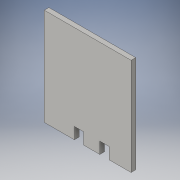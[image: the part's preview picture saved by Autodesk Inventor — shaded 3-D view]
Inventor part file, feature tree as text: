
AUTODESK INVENTOR PART (.ipt)
format: ipt  version: 2016 (Build 200138000, 138)  size: 107,520 bytes
history: native  units: in
note: dims shown in document units (in); Inventor stores cm internally (conversion verified against a paired STEP export)
features: sketch x2, extrude x1
ambient origin geometry x8: Origin, YZ Plane, XZ Plane, XY Plane, X Axis, Y Axis, Z Axis, Center Point
bodies: Solid1 (feature_tree)
feature tree (3):
  sketch  "Sketch1"  dims[d1=10.5in d2=5.125in]
  extrude  "Extrusion1"  Depth=5.125in
  sketch  "Sketch2"  dims[d3=0.875in d4=1.0in d5=0.875in d6=1.0in d7=1.25in d8=0.5in d9=0.0in]
